# Revit family: 0048817 Feilo Sylvania Lighting Fixture HYDROPROOF LED G3 600MM S 4K QC D
name_source: partatom
category: Lighting Fixtures
revit_build: Autodesk Revit 2016 (Build: 20150220_1215(x64)
units: mm (PartAtom-declared; Revit-internal decimal feet)

## family parameters
Cut with Voids When Loaded = No
Host = Face
Light Source = Yes
OmniClass Number = 23.80.70.11.14
OmniClass Title = General Luminaries, Directional
Part Type = Normal
Room Calculation Point = No
Round Connector Dimension = Use Diameter
Shared = No

## types (1)
- 0048817 HYDROPROOF LED G3 600MM S 4K QC D
    AccessoryMaterial = Diffuser-Sylvania-Glow
    Apparent Load = 14 VA
    Assembly Code = D5020200
    AssetType = Fixed
    BodyMaterial = Body-Sylvania-Gray
    BracketOffset_FEILO = 360 mm
    ClassificationName = Uniclass2015
    ClassificationValue = EF_70_80
    Color Filter = 16777215
    Cost = 0 $
    Default Elevation = 1219 mm
    Description = Hydroproof, integrated LED chemical resistant weatherproof luminaire with quick connector, with UV stabilized flat diffuser and linear prisms designed to achieve uniform lit appearance, optimise light output and to reduce glare, stainless steel diffuser clips and fixing brackets for surface and wall mounting. L 665 mm x W 110 mm x H 78 mm size, GRP housing, PMMA diffuser, DALI dimmable, 4000K, CRI80,  1900 lm, 14 W, 135 lm/W, nominal average life (h):50000, energy class: A++ A+ A Class I,IK02, IP65.
    DiffuserMaterial = Diffuser-Sylvania-Transparent
    Dimming Lamp Color Temperature Shift = <None>
    DimmingControlOptions = Dimmable
    DocumentationLiterature = http://www.sylvania-lighting.com
    DurationUnit = hours
    ElectricShockClassification = Class I
    Emit Shape Visible in Rendering = No
    Emit from Rectangle Length = 645 mm  [stored 2.11614 ft]
    Emit from Rectangle Width = 90 mm  [stored 0.295276 ft]
    ExpectedLife = 50000
    IfcExportAs = IfcLightFixtureType
    IfcExportType = IfcLightFixtureType
    ImpactProtectionIndex = IK02
    IngressProtection = IP65
    InputNominalFrequency = DC/50/60 Hz
    InputVoltage = 220-240V~
    Keynote = 16500
    Lamp = LED
    LampColourRenderingIndex = 80
    LampColourTemperature = 4000 K
    LampMacAdamStep = 3
    LampNominalLuminous = 1900 lm
    LampsType = LED
    Length = 665 mm  [stored 2.18176 ft]
    LuminousEfficacy = 135 lm/W
    Manufacturer = Feilo Sylvania
    ManufacturerName = Feilo Sylvania
    Material = grp housing, pmma diffuser
    Model = HYDROPROOF LED G3 600MM S 4K QC D
    ModelNumber = 0048817
    ModelReference = HYDROPROOF LED G3 600MM S 4K QC D
    Name = HYDROPROOF LED G3 600MM S 4K QC D
    NominalHeight = 78 mm  [stored 0.255906 ft]
    NominalLength = 665 mm  [stored 2.18176 ft]
    NominalWidth = 0 mm  [stored 0 ft]
    Photometric Web File = 0048817.ies
    PowerConsumption = 14 W
    PowerFactor = 0
    ReflectorMaterial = <By Category>
    Tilt Angle = -90.00°
    Type Image = <None>
    TypeName = HYDROPROOF LED G3 600MM S 4K QC D
    URL = http://www.sylvania-lighting.com
    Voltage = 230 V
    Weight = 1.12 kg
    Width = 110 mm  [stored 0.360892 ft]

note: [stored X ft] marks values corroborated as IEEE doubles in the binary element streams (Revit-internal decimal feet)

## geometry (parser evidence)
native form markers: Sweep x5
no freeform markers — native parametric forms only
